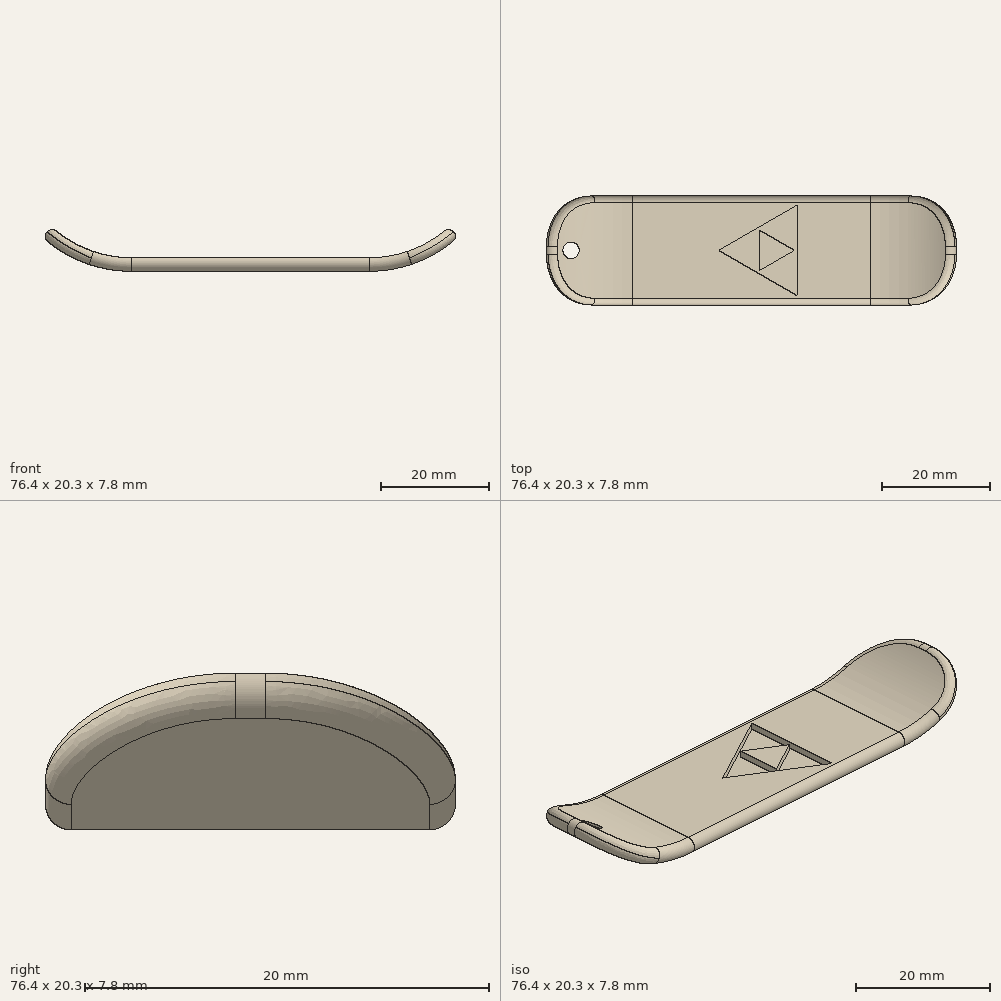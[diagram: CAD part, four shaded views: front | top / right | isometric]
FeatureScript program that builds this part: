
annotation { "Feature Type Name" : "Feature", "Feature Type Description" : "" }
export const myFeature = defineFeature(function(context is Context, id is Id, definition is map)
    precondition{}
    {
        {
            var Q0;
            Q0=qCreatedBy(makeId("Front.planeOp"),FACE);
            var sketch = newSketch(context, id + "F0", { "sketchPlane" : qUnion([Q0])});
            skLineSegment(sketch, "E0", {"start": v(-22.22, 0) * mm, "end": v(22.22, 0) * mm});
            skArc(sketch, "E1", {"start": v(-38.73, 6.39) * mm, "mid": v(-31.08, 1.65) * mm, "end": v(-22.22, 0) * mm});
            skArc(sketch, "E2.MirrorCS", {"start": v(38.73, 6.39) * mm, "mid": v(31.08, 1.65) * mm, "end": v(22.23, 0) * mm});
            skArc(sketch, "E3.0", {"start": v(37.03, 8.27) * mm, "mid": v(30.16, 4.02) * mm, "end": v(22.22, 2.54) * mm});
            skLineSegment(sketch, "E3.1", {"start": v(-22.22, 2.54) * mm, "end": v(22.22, 2.54) * mm});
            skArc(sketch, "E3.2", {"start": v(-37.03, 8.27) * mm, "mid": v(-30.16, 4.02) * mm, "end": v(-22.22, 2.54) * mm});
            skLineSegment(sketch, "E4", {"start": v(-38.73, 6.39) * mm, "end": v(-37.03, 8.27) * mm});
            skLineSegment(sketch, "E5", {"start": v(37.03, 8.27) * mm, "end": v(38.73, 6.39) * mm});
            skSolve(sketch);
        }
        {
            var Q0;
            Q0=qSketchRegion(id+"F0",true);
            extrude(context, id + "F1", {"entities" : qUnion([Q0]), "depth" : 20.32 * mm, "symmetric" : true});
        }
        {
            var Q0;
            Q0=makeQuery(id+"F1.opExtrude","CAP_EDGE",EDGE,{"disambiguationData":[OSD([sQuery(id+"F0.wireOp",EDGE,"E4")])],"isStart":false});
            var Q1;
            Q1=makeQuery(id+"F1.opExtrude","CAP_EDGE",EDGE,{"disambiguationData":[OSD([sQuery(id+"F0.wireOp",EDGE,"E4")])],"isStart":true});
            var Q2;
            Q2=makeQuery(id+"F1.opExtrude","CAP_EDGE",EDGE,{"disambiguationData":[OSD([sQuery(id+"F0.wireOp",EDGE,"E5")])],"isStart":true});
            var Q3;
            Q3=makeQuery(id+"F1.opExtrude","CAP_EDGE",EDGE,{"disambiguationData":[OSD([sQuery(id+"F0.wireOp",EDGE,"E5")])],"isStart":false});
            fillet(context, id + "F2", {"entities" : qUnion([Q0, Q1, Q2, Q3]), "radius" : 9.4 * mm, "tangentPropagation" : true, "allowEdgeOverflow" : false});
        }
        {
            var Q0;
            Q0=makeQuery(id+"F1.opExtrude","CAP_EDGE",EDGE,{"disambiguationData":[OSD([sQuery(id+"F0.wireOp",EDGE,"E3.2")])],"isStart":false});
            var Q1;
            Q1=makeQuery(id+"F2.opFillet","BLEND_EDGE",EDGE,{"blendedFrom":[makeQuery(id+"F1.opExtrude","CAP_EDGE",EDGE,{"disambiguationData":[OSD([sQuery(id+"F0.wireOp",EDGE,"E4")])],"isStart":false}),makeQuery(id+"F1.opExtrude","SWEPT_FACE",FACE,{"disambiguationData":[OSD([sQuery(id+"F0.wireOp",EDGE,"E1")])]})],"blendedInto":[makeQuery(id+"F1.opExtrude","SWEPT_FACE",FACE,{"disambiguationData":[OSD([sQuery(id+"F0.wireOp",EDGE,"E1")])]})]});
            fillet(context, id + "F3", {"entities" : qUnion([Q0, Q1]), "radius" : 1.27 * mm, "tangentPropagation" : true, "allowEdgeOverflow" : false});
        }
        {
            var Q0;
            Q0=qCreatedBy(makeId("Top.planeOp"),FACE);
            var sketch = newSketch(context, id + "F4", { "sketchPlane" : qUnion([Q0])});
            skPoint(sketch, "E6.0", {"position": v(-38.18, 0.76) * mm});
            skCircle(sketch, "E7", {"center": v(-33.61, 0) * mm, "radius": 1.52 * mm});
            skSolve(sketch);
        }
        {
            var Q0;
            Q0=qSketchRegion(id+"F4",true);
            extrude(context, id + "F5", {"entities" : qUnion([Q0]), "operationType" : NewBodyOperationType.REMOVE, "depth" : 25.4 * mm});
        }
        {
            var Q0;
            Q0=makeQuery(id+"F1.opExtrude","SWEPT_FACE",FACE,{"disambiguationData":[OSD([sQuery(id+"F0.wireOp",EDGE,"E3.1")])]});
            var sketch = newSketch(context, id + "F6", { "sketchPlane" : qUnion([Q0])});
            skLineSegment(sketch, "E8", {"start": v(8.8, -8.9) * mm, "end": v(8.8, 8.9) * mm, "construction": true});
            skLineSegment(sketch, "E9", {"start": v(8.8, 8.9) * mm, "end": v(-6.59, 0) * mm, "construction": true});
            skLineSegment(sketch, "E10", {"start": v(-6.59, 0) * mm, "end": v(8.8, -8.9) * mm, "construction": true});
            skLineSegment(sketch, "E11.0", {"start": v(8.55, -8.45) * mm, "end": v(8.55, 8.45) * mm});
            skLineSegment(sketch, "E11.1", {"start": v(-6.08, 0) * mm, "end": v(8.55, -8.45) * mm});
            skLineSegment(sketch, "E11.2", {"start": v(8.55, 8.45) * mm, "end": v(-6.08, 0) * mm});
            skLineSegment(sketch, "E12", {"start": v(1.24, -4.23) * mm, "end": v(8.55, 0) * mm, "construction": true});
            skLineSegment(sketch, "E13", {"start": v(8.55, 0) * mm, "end": v(1.24, 4.23) * mm, "construction": true});
            skLineSegment(sketch, "E14", {"start": v(1.24, 4.23) * mm, "end": v(1.24, -4.23) * mm, "construction": true});
            skLineSegment(sketch, "E15.0", {"start": v(1.5, 3.79) * mm, "end": v(1.5, -3.79) * mm});
            skLineSegment(sketch, "E15.1", {"start": v(8.05, 0) * mm, "end": v(1.5, 3.79) * mm});
            skLineSegment(sketch, "E15.2", {"start": v(1.5, -3.79) * mm, "end": v(8.05, 0) * mm});
            skSolve(sketch);
        }
        {
            var Q0;
            Q0=makeQuery(id+"F6.imprint","IMPRINT",FACE,{"disambiguationData":[TD([[makeQuery(id+"F6.imprint","IMPRINT",EDGE,{"derivedFrom":sQuery(id+"F6.wireOp",EDGE,"E11.0")}),1.0]])]});
            extrude(context, id + "F7", {"entities" : qUnion([Q0]), "operationType" : NewBodyOperationType.REMOVE, "oppositeDirection" : true, "depth" : 1.02 * mm});
        }
    });
